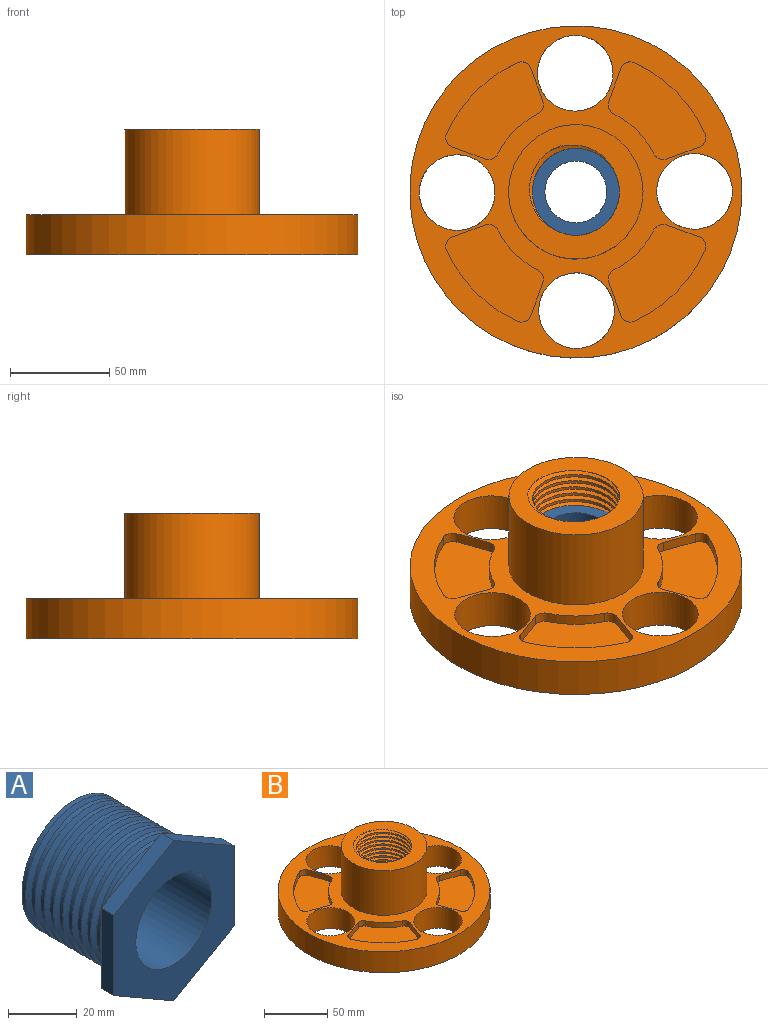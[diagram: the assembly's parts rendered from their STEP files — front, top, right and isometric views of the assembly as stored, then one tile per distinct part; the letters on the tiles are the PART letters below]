
ASSEMBLY  parts=2 mates=1
PART A: 14 faces, bbox 52x44.9x58.4 mm
  f0: cylinder r=21.93mm len=43.87mm, axis (0,-1,0), area 1732.9mm2, adj f1,f10,f11,f12,f13
  f1: plane 43.86x43.64mm, normal (0,1,0), area 648.8mm2, adj f0,f2,f12,f13
  f2: cylinder r=15.58mm len=41.95mm, axis (0,-1,0), area 4106.9mm2, adj f1,f9
  f3: plane 28.53x5.08mm, normal (1,0,0), area 144.9mm2, adj f4,f8,f9,f10
  f4: plane 24.71x14.27mm, normal (0.5,0,0.87), area 144.9mm2, adj f3,f5,f9,f10
  f5: plane 24.71x14.27mm, normal (-0.5,0,0.87), area 144.9mm2, adj f4,f6,f9,f10
  f6: plane 28.53x5.08mm, normal (-1,0,0), area 144.9mm2, adj f5,f7,f9,f10
  f7: plane 24.71x14.27mm, normal (-0.5,0,-0.87), area 144.9mm2, adj f6,f8,f9,f10
  f8: plane 24.71x14.27mm, normal (0.5,0,-0.87), area 144.9mm2, adj f3,f7,f9,f10
  f9: plane 57.07x49.42mm, normal (0,-1,0), area 1352.3mm2, adj f2,f3,f4,f5,f6,f7,f8
  f10: plane 57.07x49.42mm, normal (0,1,0), area 603.9mm2, adj f0,f3,f4,f5,f6,f7,f8
  f11: plane 2.52x2.28mm, normal (-1,0.03,-0.06), area 2.9mm2, adj f0,f12,f13
  f12: bspline ~50.65x43.87mm, area 3434.4mm2, adj f0,f1,f11,f13
  f13: bspline ~50.74x44.01mm, area 3299.2mm2, adj f0,f1,f11,f12
PART B: 49 faces, bbox 168.6x168.6x66 mm
  f0: plane 167.24x167.24mm, normal (0,0,1), area 8322.2mm2, adj f4,f5,f6,f7,f8,f9,f10,f11
  f1: plane 68.98x68.98mm, normal (0,0,1), area 1976.9mm2, adj f2,f5,f47,f48
  f2: cylinder r=21.93mm len=63.19mm, axis (0,0,1), area 3779.9mm2, adj f1,f3,f46,f47,f48
  f3: plane 167.24x167.24mm, normal (0,0,-1), area 15896mm2, adj f2,f4,f6,f7,f8,f9
  f4: cylinder r=83.62mm len=167.24mm, axis (0,0,1), area 10603.9mm2, adj f0,f3
  f5: cylinder r=33.83mm len=67.66mm, axis (0,0,1), area 9142.2mm2, adj f0,f1
  f6: cylinder r=19.05mm len=38.1mm, axis (0,0,1), area 2415.7mm2, adj f0,f3
  f7: cylinder r=19.05mm len=38.1mm, axis (0,0,1), area 2415.7mm2, adj f0,f3
  f8: cylinder r=19.05mm len=38.1mm, axis (0,0,1), area 2415.7mm2, adj f0,f3
  f9: cylinder r=19.05mm len=38.1mm, axis (0,0,1), area 2415.7mm2, adj f0,f3
  f10: cylinder r=43.69mm len=20.14mm, axis (0,0,1), area 147.4mm2, adj f0,f14,f42,f45
  f11: plane 16.6x6.04mm, normal (-0.34,0.94,0), area 89.7mm2, adj f0,f14,f44,f45
  f12: cylinder r=71.44mm len=35.57mm, axis (0,0,1), area 261.1mm2, adj f0,f14,f43,f44
  f13: plane 16.6x6.04mm, normal (0.94,-0.34,0), area 89.7mm2, adj f0,f14,f42,f43
  f14: plane 49.24x49.24mm, normal (0,0,1), area 1372.3mm2, adj f10,f11,f12,f13,f42,f43,f44,f45
  f15: cylinder r=43.69mm len=20.14mm, axis (0,0,1), area 147.4mm2, adj f0,f19,f38,f41
  f16: plane 16.6x6.04mm, normal (0.94,0.34,0), area 89.7mm2, adj f0,f19,f38,f39
  f17: cylinder r=71.44mm len=35.57mm, axis (0,0,1), area 261.1mm2, adj f0,f19,f39,f40
  f18: plane 16.6x6.04mm, normal (-0.34,-0.94,0), area 89.7mm2, adj f0,f19,f40,f41
  f19: plane 49.24x49.24mm, normal (0,0,1), area 1372.3mm2, adj f15,f16,f17,f18,f38,f39,f40,f41
  f20: cylinder r=43.69mm len=20.14mm, axis (0,0,1), area 147.4mm2, adj f0,f24,f34,f37
  f21: plane 16.6x6.04mm, normal (0.34,-0.94,0), area 89.7mm2, adj f0,f24,f36,f37
  f22: cylinder r=71.44mm len=35.57mm, axis (0,0,1), area 261.1mm2, adj f0,f24,f35,f36
  f23: plane 16.6x6.04mm, normal (-0.94,0.34,0), area 89.7mm2, adj f0,f24,f34,f35
  f24: plane 49.24x49.24mm, normal (0,0,1), area 1372.3mm2, adj f20,f21,f22,f23,f34,f35,f36,f37
  f25: cylinder r=43.69mm len=20.14mm, axis (0,0,1), area 147.4mm2, adj f0,f29,f30,f33
  f26: plane 16.6x6.04mm, normal (-0.94,-0.34,0), area 89.7mm2, adj f0,f29,f32,f33
  f27: cylinder r=71.44mm len=35.57mm, axis (0,0,1), area 261.1mm2, adj f0,f29,f31,f32
  f28: plane 16.6x6.04mm, normal (0.34,0.94,0), area 89.7mm2, adj f0,f29,f30,f31
  f29: plane 49.24x49.24mm, normal (0,0,1), area 1372.3mm2, adj f25,f26,f27,f28,f30,f31,f32,f33
  f30: cylinder r=5.08mm len=6.3mm, axis (0,0,1), area 37.8mm2, adj f0,f25,f28,f29
  f31: cylinder r=5.08mm len=6.87mm, axis (0,0,1), area 42.5mm2, adj f0,f27,f28,f29
  f32: cylinder r=5.08mm len=6.87mm, axis (0,0,1), area 42.5mm2, adj f0,f26,f27,f29
  f33: cylinder r=5.08mm len=6.3mm, axis (0,0,1), area 37.8mm2, adj f0,f25,f26,f29
  f34: cylinder r=5.08mm len=6.3mm, axis (0,0,1), area 37.8mm2, adj f0,f20,f23,f24
  f35: cylinder r=5.08mm len=6.87mm, axis (0,0,1), area 42.5mm2, adj f0,f22,f23,f24
  f36: cylinder r=5.08mm len=6.87mm, axis (0,0,1), area 42.5mm2, adj f0,f21,f22,f24
  f37: cylinder r=5.08mm len=6.3mm, axis (0,0,1), area 37.8mm2, adj f0,f20,f21,f24
  f38: cylinder r=5.08mm len=6.3mm, axis (0,0,1), area 37.8mm2, adj f0,f15,f16,f19
  f39: cylinder r=5.08mm len=6.87mm, axis (0,0,1), area 42.5mm2, adj f0,f16,f17,f19
  f40: cylinder r=5.08mm len=6.87mm, axis (0,0,1), area 42.5mm2, adj f0,f17,f18,f19
  f41: cylinder r=5.08mm len=6.3mm, axis (0,0,1), area 37.8mm2, adj f0,f15,f18,f19
  f42: cylinder r=5.08mm len=6.3mm, axis (0,0,1), area 37.8mm2, adj f0,f10,f13,f14
  f43: cylinder r=5.08mm len=6.87mm, axis (0,0,1), area 42.5mm2, adj f0,f12,f13,f14
  f44: cylinder r=5.08mm len=6.87mm, axis (0,0,1), area 42.5mm2, adj f0,f11,f12,f14
  f45: cylinder r=5.08mm len=6.3mm, axis (0,0,1), area 37.8mm2, adj f0,f10,f11,f14
  f46: plane 2.27x2.2mm, normal (-0.5,0.87,0.03), area 2.9mm2, adj f2,f47,f48
  f47: bspline ~64.68x56.47mm, area 6683mm2, adj f1,f2,f46,f48
  f48: bspline ~63.33x56.47mm, area 6451.3mm2, adj f1,f2,f46,f47
PLACE A rot(axis=(-1,0,0),90deg) t=(-70.79,-104.8,-61.95)mm
PLACE B t=(-48.86,-104.8,-24.09)mm fixed
MATE revolute B.f2 <-> A.f0  axis (0,0,-1) through (-70.79,-104.8,-61.95)mm
